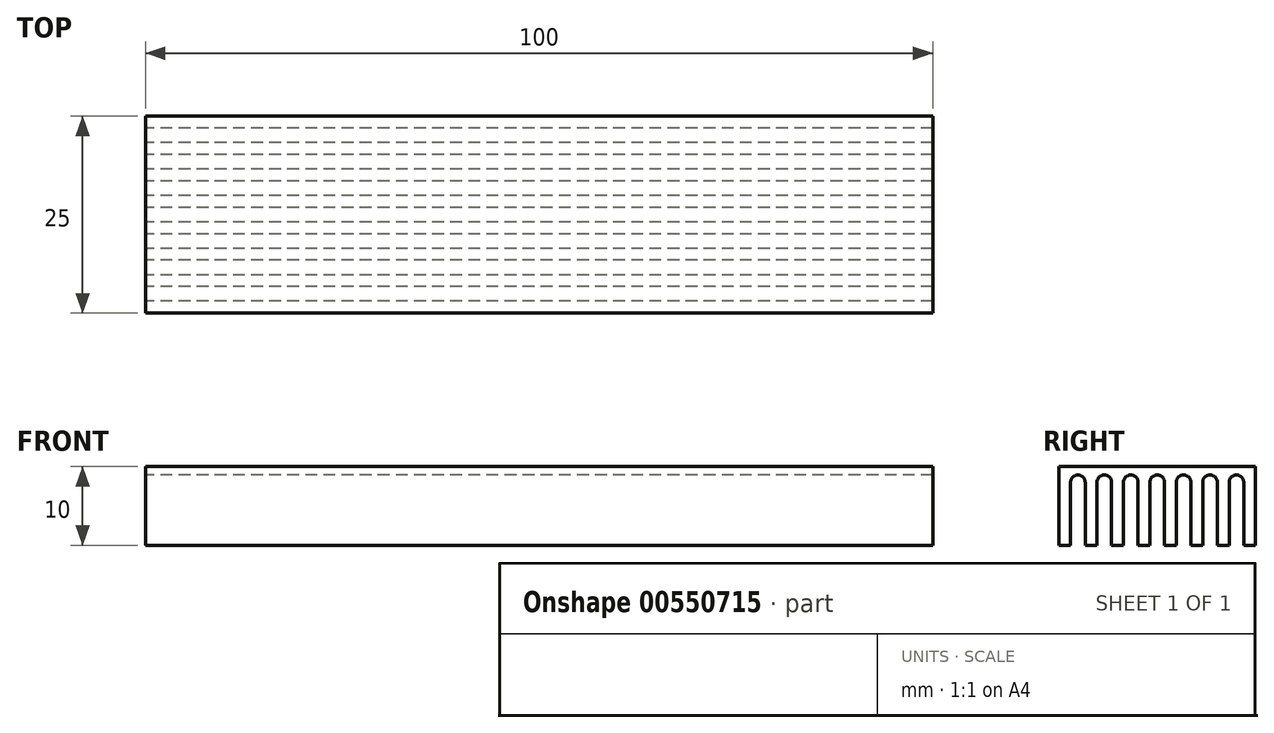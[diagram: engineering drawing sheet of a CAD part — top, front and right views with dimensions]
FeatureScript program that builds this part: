
annotation { "Feature Type Name" : "Feature", "Feature Type Description" : "" }
export const myFeature = defineFeature(function(context is Context, id is Id, definition is map)
    precondition{}
    {
        {
            var Q0;
            Q0=qCreatedBy(makeId("Right.planeOp"),FACE);
            var sketch = newSketch(context, id + "F0", { "sketchPlane" : qUnion([Q0])});
            skLineSegment(sketch, "E0.rect.bottom", {"start": v(-2.43, 4) * mm, "end": v(-0.93, 4) * mm});
            skLineSegment(sketch, "E0.rect.top", {"start": v(-2.43, -4) * mm, "end": v(-0.93, -4) * mm});
            skLineSegment(sketch, "E0.rect.left", {"start": v(-2.43, 4) * mm, "end": v(-2.43, -4) * mm});
            skLineSegment(sketch, "E0.rect.right", {"start": v(-0.93, 4) * mm, "end": v(-0.93, -4) * mm});
            skPoint(sketch, "E0.rect.middle", {"position": v(-1.68, 0) * mm});
            skLineSegment(sketch, "E1.rect.bottom", {"start": v(0.93, 4) * mm, "end": v(2.43, 4) * mm});
            skLineSegment(sketch, "E1.rect.top", {"start": v(0.93, -4) * mm, "end": v(2.43, -4) * mm});
            skLineSegment(sketch, "E1.rect.left", {"start": v(0.93, 4) * mm, "end": v(0.93, -4) * mm});
            skLineSegment(sketch, "E1.rect.right", {"start": v(2.43, 4) * mm, "end": v(2.43, -4) * mm});
            skPoint(sketch, "E1.rect.middle", {"position": v(1.68, 0) * mm});
            skLineSegment(sketch, "E2.rect.bottom", {"start": v(-5.79, 4) * mm, "end": v(-4.29, 4) * mm});
            skLineSegment(sketch, "E2.rect.top", {"start": v(-5.79, -4) * mm, "end": v(-4.29, -4) * mm});
            skLineSegment(sketch, "E2.rect.left", {"start": v(-5.79, 4) * mm, "end": v(-5.79, -4) * mm});
            skLineSegment(sketch, "E2.rect.right", {"start": v(-4.29, 4) * mm, "end": v(-4.29, -4) * mm});
            skPoint(sketch, "E2.rect.middle", {"position": v(-5.04, 0) * mm});
            skLineSegment(sketch, "E3.rect.bottom", {"start": v(-9.14, 4) * mm, "end": v(-7.64, 4) * mm});
            skLineSegment(sketch, "E3.rect.top", {"start": v(-9.14, -4) * mm, "end": v(-7.64, -4) * mm});
            skLineSegment(sketch, "E3.rect.left", {"start": v(-9.14, 4) * mm, "end": v(-9.14, -4) * mm});
            skLineSegment(sketch, "E3.rect.right", {"start": v(-7.64, 4) * mm, "end": v(-7.64, -4) * mm});
            skPoint(sketch, "E3.rect.middle", {"position": v(-8.4, 0) * mm});
            skLineSegment(sketch, "E4.rect.bottom", {"start": v(4.29, 4) * mm, "end": v(5.79, 4) * mm});
            skLineSegment(sketch, "E4.rect.top", {"start": v(4.29, -4) * mm, "end": v(5.79, -4) * mm});
            skLineSegment(sketch, "E4.rect.left", {"start": v(4.29, 4) * mm, "end": v(4.29, -4) * mm});
            skLineSegment(sketch, "E4.rect.right", {"start": v(5.79, 4) * mm, "end": v(5.79, -4) * mm});
            skPoint(sketch, "E4.rect.middle", {"position": v(5.04, 0) * mm});
            skLineSegment(sketch, "E5.rect.bottom", {"start": v(7.64, 4) * mm, "end": v(9.14, 4) * mm});
            skLineSegment(sketch, "E5.rect.top", {"start": v(7.64, -4) * mm, "end": v(9.14, -4) * mm});
            skLineSegment(sketch, "E5.rect.left", {"start": v(7.64, 4) * mm, "end": v(7.64, -4) * mm});
            skLineSegment(sketch, "E5.rect.right", {"start": v(9.14, 4) * mm, "end": v(9.14, -4) * mm});
            skPoint(sketch, "E5.rect.middle", {"position": v(8.4, 0) * mm});
            skLineSegment(sketch, "E6.rect.bottom", {"start": v(11, 4) * mm, "end": v(12.5, 4) * mm});
            skLineSegment(sketch, "E6.rect.top", {"start": v(11, -4) * mm, "end": v(12.5, -4) * mm});
            skLineSegment(sketch, "E6.rect.left", {"start": v(11, 4) * mm, "end": v(11, -4) * mm});
            skLineSegment(sketch, "E6.rect.right", {"start": v(12.5, 4) * mm, "end": v(12.5, -4) * mm});
            skPoint(sketch, "E6.rect.middle", {"position": v(11.75, 0) * mm});
            skLineSegment(sketch, "E7.rect.bottom", {"start": v(-12.5, 4) * mm, "end": v(-11, 4) * mm});
            skLineSegment(sketch, "E7.rect.top", {"start": v(-12.5, -4) * mm, "end": v(-11, -4) * mm});
            skLineSegment(sketch, "E7.rect.left", {"start": v(-12.5, 4) * mm, "end": v(-12.5, -4) * mm});
            skLineSegment(sketch, "E7.rect.right", {"start": v(-11, 4) * mm, "end": v(-11, -4) * mm});
            skPoint(sketch, "E7.rect.middle", {"position": v(-11.75, 0) * mm});
            skLineSegment(sketch, "E8", {"start": v(-11, -4) * mm, "end": v(-9.14, -4) * mm, "construction": true});
            skLineSegment(sketch, "E9", {"start": v(-7.64, -4) * mm, "end": v(-5.79, -4) * mm, "construction": true});
            skLineSegment(sketch, "E10", {"start": v(-4.29, -4) * mm, "end": v(-2.43, -4) * mm, "construction": true});
            skLineSegment(sketch, "E11", {"start": v(2.43, -4) * mm, "end": v(4.29, -4) * mm, "construction": true});
            skLineSegment(sketch, "E12", {"start": v(5.79, -4) * mm, "end": v(7.64, -4) * mm, "construction": true});
            skLineSegment(sketch, "E13", {"start": v(9.14, -4) * mm, "end": v(11, -4) * mm, "construction": true});
            skLineSegment(sketch, "E14", {"start": v(-0.93, -4) * mm, "end": v(0, -4) * mm, "construction": true});
            skLineSegment(sketch, "E15", {"start": v(0.93, -4) * mm, "end": v(0, -4) * mm, "construction": true});
            skArc(sketch, "E16", {"start": v(-2.43, 4) * mm, "mid": v(-3.36, 4.93) * mm, "end": v(-4.29, 4) * mm});
            skArc(sketch, "E17", {"start": v(-5.79, 4) * mm, "mid": v(-6.71, 4.93) * mm, "end": v(-7.64, 4) * mm});
            skArc(sketch, "E18", {"start": v(-9.14, 4) * mm, "mid": v(-10.07, 4.93) * mm, "end": v(-11, 4) * mm});
            skArc(sketch, "E19.0.MirrorCS", {"start": v(2.43, 4) * mm, "mid": v(3.36, 4.93) * mm, "end": v(4.29, 4) * mm});
            skArc(sketch, "E20.0.MirrorCS", {"start": v(5.79, 4) * mm, "mid": v(6.71, 4.93) * mm, "end": v(7.64, 4) * mm});
            skArc(sketch, "E21.0.MirrorCS", {"start": v(9.14, 4) * mm, "mid": v(10.07, 4.93) * mm, "end": v(11, 4) * mm});
            skLineSegment(sketch, "E22", {"start": v(-12.5, 4) * mm, "end": v(-12.5, 6) * mm});
            skLineSegment(sketch, "E23", {"start": v(-12.5, 6) * mm, "end": v(12.5, 6) * mm});
            skLineSegment(sketch, "E24", {"start": v(12.5, 6) * mm, "end": v(12.5, 4) * mm});
            skLineSegment(sketch, "E25", {"start": v(-10.07, 4.93) * mm, "end": v(10.07, 4.93) * mm, "construction": true});
            skArc(sketch, "E26", {"start": v(0.93, 4) * mm, "mid": v(0, 4.93) * mm, "end": v(-0.93, 4) * mm});
            skSolve(sketch);
        }
        {
            var Q0;
            Q0=makeQuery(id+"F0.imprint","IMPRINT",FACE,{"disambiguationData":[TD([[makeQuery(id+"F0.imprint","IMPRINT",EDGE,{"derivedFrom":sQuery(id+"F0.wireOp",EDGE,"E0.rect.bottom")}),1.0]])]});
            var Q1;
            Q1=makeQuery(id+"F0.imprint","IMPRINT",FACE,{"disambiguationData":[TD([[makeQuery(id+"F0.imprint","IMPRINT",EDGE,{"derivedFrom":sQuery(id+"F0.wireOp",EDGE,"E7.rect.bottom")}),-1.0]])]});
            var Q2;
            Q2=makeQuery(id+"F0.imprint","IMPRINT",FACE,{"disambiguationData":[TD([[makeQuery(id+"F0.imprint","IMPRINT",EDGE,{"derivedFrom":sQuery(id+"F0.wireOp",EDGE,"E3.rect.bottom")}),-1.0]])]});
            var Q3;
            Q3=makeQuery(id+"F0.imprint","IMPRINT",FACE,{"disambiguationData":[TD([[makeQuery(id+"F0.imprint","IMPRINT",EDGE,{"derivedFrom":sQuery(id+"F0.wireOp",EDGE,"E2.rect.bottom")}),-1.0]])]});
            var Q4;
            Q4=makeQuery(id+"F0.imprint","IMPRINT",FACE,{"disambiguationData":[TD([[makeQuery(id+"F0.imprint","IMPRINT",EDGE,{"derivedFrom":sQuery(id+"F0.wireOp",EDGE,"E0.rect.bottom")}),-1.0]])]});
            var Q5;
            Q5=makeQuery(id+"F0.imprint","IMPRINT",FACE,{"disambiguationData":[TD([[makeQuery(id+"F0.imprint","IMPRINT",EDGE,{"derivedFrom":sQuery(id+"F0.wireOp",EDGE,"E1.rect.bottom")}),-1.0]])]});
            var Q6;
            Q6=makeQuery(id+"F0.imprint","IMPRINT",FACE,{"disambiguationData":[TD([[makeQuery(id+"F0.imprint","IMPRINT",EDGE,{"derivedFrom":sQuery(id+"F0.wireOp",EDGE,"E4.rect.bottom")}),-1.0]])]});
            var Q7;
            Q7=makeQuery(id+"F0.imprint","IMPRINT",FACE,{"disambiguationData":[TD([[makeQuery(id+"F0.imprint","IMPRINT",EDGE,{"derivedFrom":sQuery(id+"F0.wireOp",EDGE,"E5.rect.bottom")}),-1.0]])]});
            var Q8;
            Q8=makeQuery(id+"F0.imprint","IMPRINT",FACE,{"disambiguationData":[TD([[makeQuery(id+"F0.imprint","IMPRINT",EDGE,{"derivedFrom":sQuery(id+"F0.wireOp",EDGE,"E6.rect.bottom")}),-1.0]])]});
            extrude(context, id + "F1", {"entities" : qUnion([Q0, Q1, Q2, Q3, Q4, Q5, Q6, Q7, Q8]), "depth" : 100 * mm, "symmetric" : true});
        }
    });
